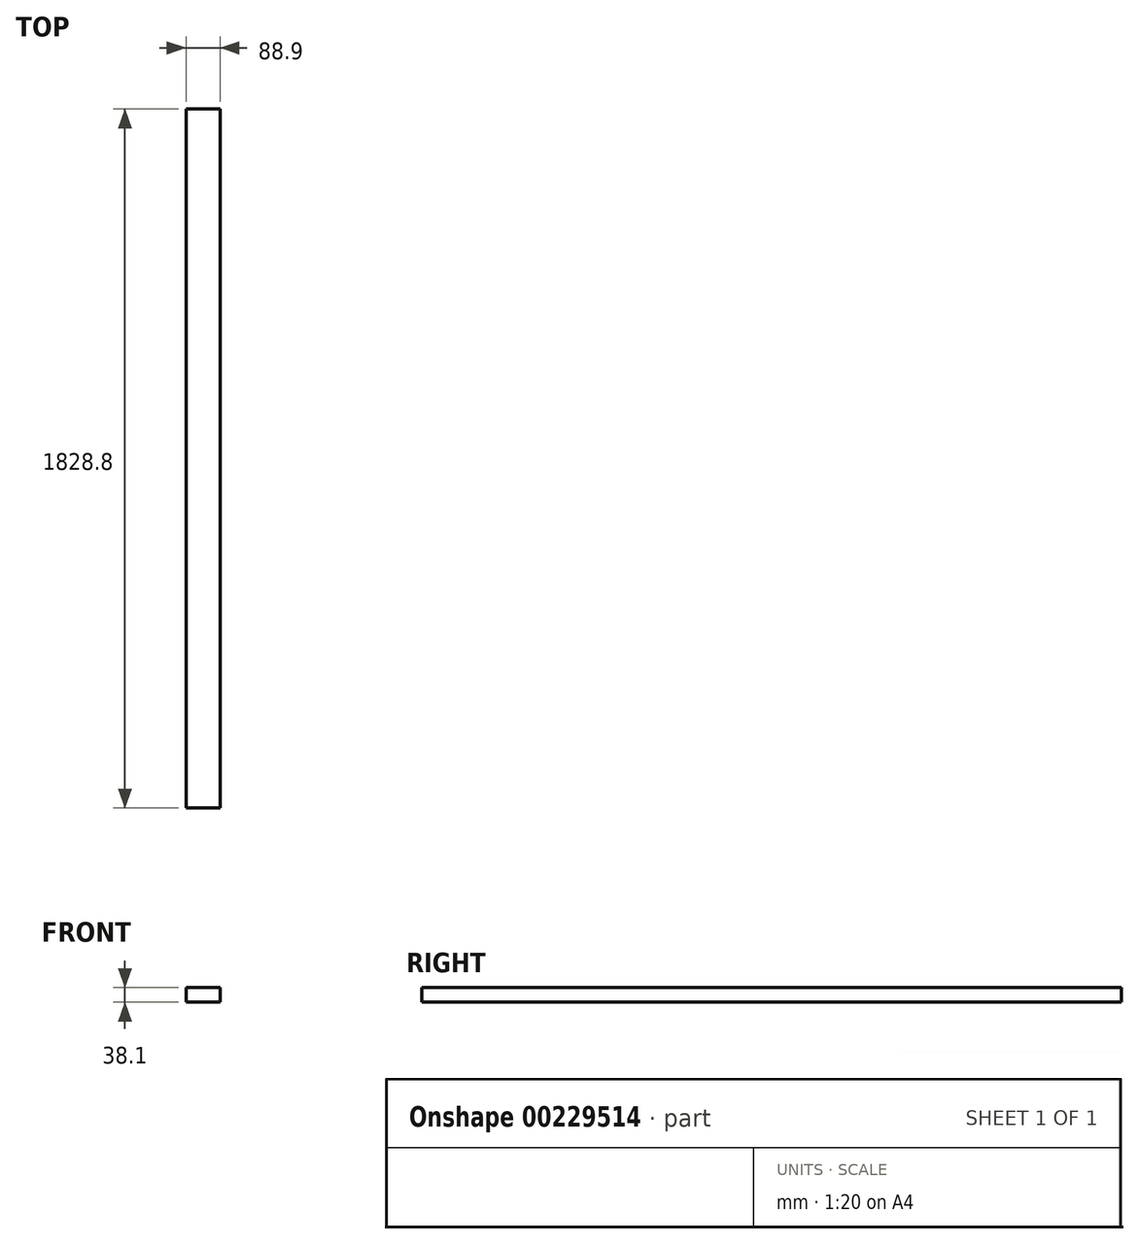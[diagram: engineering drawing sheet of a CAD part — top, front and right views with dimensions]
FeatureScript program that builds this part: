
annotation { "Feature Type Name" : "Feature", "Feature Type Description" : "" }
export const myFeature = defineFeature(function(context is Context, id is Id, definition is map)
    precondition{}
    {
        {
            var Q0;
            Q0=qCreatedBy(makeId("Front.planeOp"),FACE);
            var sketch = newSketch(context, id + "F0", { "sketchPlane" : qUnion([Q0])});
            skLineSegment(sketch, "E0.bottom", {"start": v(0, 0) * mm, "end": v(88.9, 0) * mm});
            skLineSegment(sketch, "E0.top", {"start": v(0, -38.1) * mm, "end": v(88.9, -38.1) * mm});
            skLineSegment(sketch, "E0.left", {"start": v(0, 0) * mm, "end": v(0, -38.1) * mm});
            skLineSegment(sketch, "E0.right", {"start": v(88.9, 0) * mm, "end": v(88.9, -38.1) * mm});
            skSolve(sketch);
        }
        {
            var Q0;
            Q0=qSketchRegion(id+"F0",true);
            extrude(context, id + "F1", {"entities" : qUnion([Q0]), "depth" : 1828.8 * mm});
        }
    });
